# Revit family: VLGFP1501-xxxWS8xxR0xxx
name_source: partatom
category: Oprawy oświetleniowe
revit_build: Autodesk Revit 2017 (Build: 20190507_1515(x64)
units: mm (PartAtom-declared; Revit-internal decimal feet)

## family parameters
Numer OmniClass = 23.80.70.11
Obiekt nadrzędny = Powierzchnia
Punkt obliczania pomieszczeń = Nie
Tnij formami wycięć po wczytaniu = Nie
Typ części = Normalny
Tytuł OmniClass = Luminaries for Internal Lighting
Współdzielony = Nie
Wymiar okrągłego złącza = Użyj średnicy
Źródło światła = Tak

## types (10) — shared parameters
Emituj kształt widoczny w renderingu = Nie
Emituj z długości prostokąta = 63 mm  [stored 0.206693 ft]
Emituj z szerokości prostokąta = 1469 mm  [stored 4.81955 ft]
Filtr koloru = 16777215
Kod zespołu = D5020200
Lampa = LED
Odchylenie kierunku = 90.00°
Plik sieci fotometrycznej = VLGFP1501-5NDWS840R0800.IES
Producent = RIDI Leuchten GmbH
URL = www.ridi.de
Zmiana temperatury barwowej przyciemniania lampy = <Brak>
brand = RIDI
conformity mark = CE
electrical safety class = 1
height = 66 mm  [stored 0.216535 ft]
ingress protection (IP) code = IP54
length = 1500 mm  [stored 4.92126 ft]
nominal frequency = 50-60Hz
nominal voltage = 230
voltage type (AC, DC, UC) = AC
weight = 1.9 kg
width = 67 mm
zero-valued in all types: Domyślna rzędna

## per-type parameters (varying)
| type | Model | Obciążenie pozorne | rated input power |
| VLGFP1501-5NDWS830R0400 | 1551151 | 28 VA | 28 |
| VLGFP1501-7DAWS830R0400 | 1561151 | 28 VA | 28 |
| VLGFP1501-5NDWS830R0750 | 1551032 | 55 VA | 55 |
| VLGFP1501-7DAWS830R0750 | 1561032 | 55 VA | 55 |
| VLGFP1501-5NDWS830R0750-RF | 1551119 | 55 VA | 55 |
| VLGFP1501-5NDWS840R0450 | 1551147 | 28 VA | 28 |
| VLGFP1501-7DAWS840R0450 | 1561147 | 28 VA | 28 |
| VLGFP1501-5NDWS840R0800 | 1551012 | 55 VA | 55 |
| VLGFP1501-7DAWS840R0800 | 1561012 | 55 VA | 55 |
| VLGFP1501-5NDWS840R0800-RF | 1551120 | 55 VA | 55 |

note: column(s) folded — value = type name in every type: product name

note: [stored X ft] marks values corroborated as IEEE doubles in the binary element streams (Revit-internal decimal feet)
